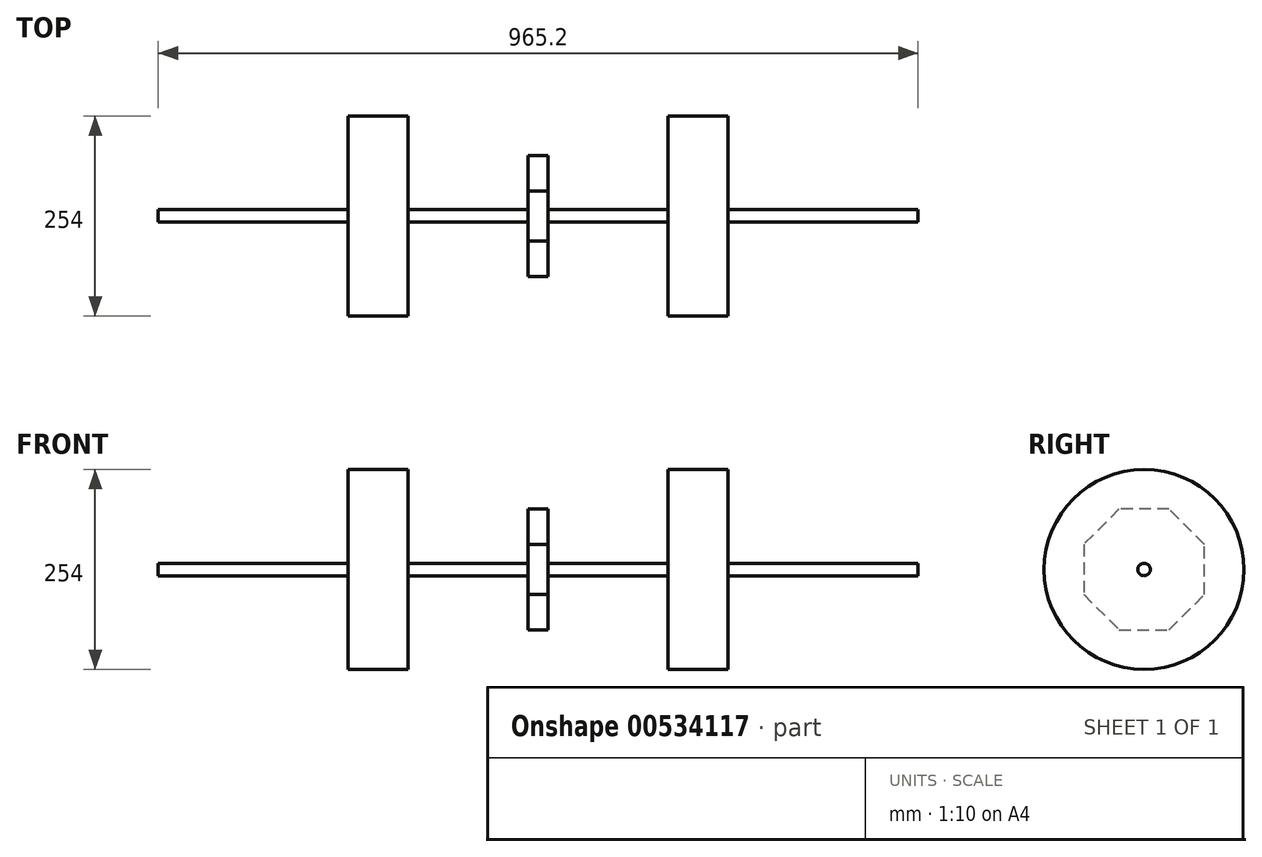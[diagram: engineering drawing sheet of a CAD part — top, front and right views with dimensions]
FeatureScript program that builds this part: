
annotation { "Feature Type Name" : "Feature", "Feature Type Description" : "" }
export const myFeature = defineFeature(function(context is Context, id is Id, definition is map)
    precondition{}
    {
        {
            var Q0;
            Q0=qCreatedBy(makeId("Right.planeOp"),FACE);
            var sketch = newSketch(context, id + "F0", { "sketchPlane" : qUnion([Q0])});
            skLineSegment(sketch, "E0", {"start": v(0, 0) * mm, "end": v(0, -63.5) * mm});
            skLineSegment(sketch, "E1", {"start": v(0, -63.5) * mm, "end": v(44.9, -108.4) * mm});
            skLineSegment(sketch, "E2", {"start": v(44.9, -108.4) * mm, "end": v(108.4, -108.4) * mm});
            skLineSegment(sketch, "E3", {"start": v(108.4, -108.4) * mm, "end": v(153.3, -63.5) * mm});
            skLineSegment(sketch, "E4", {"start": v(153.3, -63.5) * mm, "end": v(153.3, 0) * mm});
            skLineSegment(sketch, "E5", {"start": v(153.3, 0) * mm, "end": v(108.4, 44.9) * mm});
            skLineSegment(sketch, "E6", {"start": v(108.4, 44.9) * mm, "end": v(44.9, 44.9) * mm});
            skLineSegment(sketch, "E7", {"start": v(44.9, 44.9) * mm, "end": v(0, 0) * mm});
            skSolve(sketch);
        }
        {
            var Q0;
            Q0=makeQuery(id+"F0.imprint","IMPRINT",FACE,{"disambiguationData":[TD([[makeQuery(id+"F0.imprint","IMPRINT",EDGE,{"derivedFrom":sQuery(id+"F0.wireOp",EDGE,"E0")}),1.0]])]});
            extrude(context, id + "F1", {"entities" : qUnion([Q0]), "depth" : 25.4 * mm, "offsetDistance" : 25.4 * mm});
        }
        {
            var Q0;
            Q0=makeQuery(id+"F1.opExtrude","CAP_FACE",FACE,{"disambiguationData":[OSD([sQuery(id+"F0.wireOp",EDGE,"E0"),sQuery(id+"F0.wireOp",EDGE,"E1"),sQuery(id+"F0.wireOp",EDGE,"E2"),sQuery(id+"F0.wireOp",EDGE,"E3"),sQuery(id+"F0.wireOp",EDGE,"E4"),sQuery(id+"F0.wireOp",EDGE,"E5"),sQuery(id+"F0.wireOp",EDGE,"E6"),sQuery(id+"F0.wireOp",EDGE,"E7")])],"isStart":false});
            var sketch = newSketch(context, id + "F2", { "sketchPlane" : qUnion([Q0])});
            skCircle(sketch, "E8", {"center": v(76.65, -31.75) * mm, "radius": 7.94 * mm});
            skPoint(sketch, "E8.centerSnap0", {"position": v(153.3, -31.75) * mm});
            skPoint(sketch, "E8.centerSnap1", {"position": v(76.65, 44.9) * mm});
            skSolve(sketch);
        }
        {
            var Q0;
            Q0=makeQuery(id+"F2.imprint","IMPRINT",FACE,{"disambiguationData":[TD([[makeQuery(id+"F2.imprint","IMPRINT",EDGE,{"derivedFrom":sQuery(id+"F2.wireOp",EDGE,"E8")}),1.0]])]});
            extrude(context, id + "F3", {"entities" : qUnion([Q0]), "operationType" : NewBodyOperationType.ADD, "depth" : 152.4 * mm, "offsetDistance" : 25.4 * mm});
        }
        {
            var Q0;
            Q0=makeQuery(id+"F3.opExtrude","CAP_FACE",FACE,{"disambiguationData":[OSD([sQuery(id+"F2.wireOp",EDGE,"E8")])],"isStart":false});
            var sketch = newSketch(context, id + "F4", { "sketchPlane" : qUnion([Q0])});
            skCircle(sketch, "E9", {"center": v(76.65, -31.75) * mm, "radius": 127 * mm});
            skSolve(sketch);
        }
        {
            var Q0;
            Q0 = qSketchRegion(id + "F4", true);
            extrude(context, id + "F5", {"entities" : qUnion([Q0]), "operationType" : NewBodyOperationType.ADD, "depth" : 76.2 * mm, "offsetDistance" : 25.4 * mm});
        }
        {
            var Q0;
            Q0=makeQuery(id+"F5.opExtrude","CAP_FACE",FACE,{"disambiguationData":[OSD([sQuery(id+"F4.wireOp",EDGE,"E9")])],"isStart":false});
            var sketch = newSketch(context, id + "F6", { "sketchPlane" : qUnion([Q0])});
            skCircle(sketch, "E10", {"center": v(76.65, -31.75) * mm, "radius": 7.94 * mm});
            skSolve(sketch);
        }
        {
            var Q0;
            Q0=makeQuery(id+"F6.imprint","IMPRINT",FACE,{"disambiguationData":[TD([[makeQuery(id+"F6.imprint","IMPRINT",EDGE,{"derivedFrom":sQuery(id+"F6.wireOp",EDGE,"E10")}),1.0]])]});
            extrude(context, id + "F7", {"entities" : qUnion([Q0]), "operationType" : NewBodyOperationType.ADD, "depth" : 241.3 * mm, "offsetDistance" : 25.4 * mm});
        }
        {
            var Q0;
            Q0=makeQuery(id+"F1.opExtrude","CAP_FACE",FACE,{"disambiguationData":[OSD([sQuery(id+"F0.wireOp",EDGE,"E0"),sQuery(id+"F0.wireOp",EDGE,"E1"),sQuery(id+"F0.wireOp",EDGE,"E2"),sQuery(id+"F0.wireOp",EDGE,"E3"),sQuery(id+"F0.wireOp",EDGE,"E4"),sQuery(id+"F0.wireOp",EDGE,"E5"),sQuery(id+"F0.wireOp",EDGE,"E6"),sQuery(id+"F0.wireOp",EDGE,"E7")])],"isStart":true});
            var sketch = newSketch(context, id + "F8", { "sketchPlane" : qUnion([Q0])});
            skCircle(sketch, "E11", {"center": v(-76.65, -31.75) * mm, "radius": 7.94 * mm});
            skPoint(sketch, "E11.centerSnap0", {"position": v(0, -31.75) * mm});
            skPoint(sketch, "E11.centerSnap1", {"position": v(-76.65, 44.9) * mm});
            skSolve(sketch);
        }
        {
            var Q0;
            Q0 = qSketchRegion(id + "F8", true);
            extrude(context, id + "F9", {"entities" : qUnion([Q0]), "operationType" : NewBodyOperationType.ADD, "depth" : 152.4 * mm, "offsetDistance" : 25.4 * mm});
        }
        {
            var Q0;
            Q0=makeQuery(id+"F9.opExtrude","CAP_FACE",FACE,{"disambiguationData":[OSD([sQuery(id+"F8.wireOp",EDGE,"E11")])],"isStart":false});
            var sketch = newSketch(context, id + "F10", { "sketchPlane" : qUnion([Q0])});
            skCircle(sketch, "E12", {"center": v(-76.65, -31.75) * mm, "radius": 127 * mm});
            skSolve(sketch);
        }
        {
            var Q0;
            Q0 = qSketchRegion(id + "F10", true);
            extrude(context, id + "F11", {"entities" : qUnion([Q0]), "operationType" : NewBodyOperationType.ADD, "depth" : 76.2 * mm, "offsetDistance" : 25.4 * mm});
        }
        {
            var Q0;
            Q0=makeQuery(id+"F11.opExtrude","CAP_FACE",FACE,{"disambiguationData":[OSD([sQuery(id+"F10.wireOp",EDGE,"E12")])],"isStart":false});
            var sketch = newSketch(context, id + "F12", { "sketchPlane" : qUnion([Q0])});
            skCircle(sketch, "E13", {"center": v(-76.65, -31.75) * mm, "radius": 7.94 * mm});
            skSolve(sketch);
        }
        {
            var Q0;
            Q0 = qSketchRegion(id + "F12", true);
            extrude(context, id + "F13", {"entities" : qUnion([Q0]), "operationType" : NewBodyOperationType.ADD, "depth" : 241.3 * mm, "offsetDistance" : 25.4 * mm});
        }
    });
